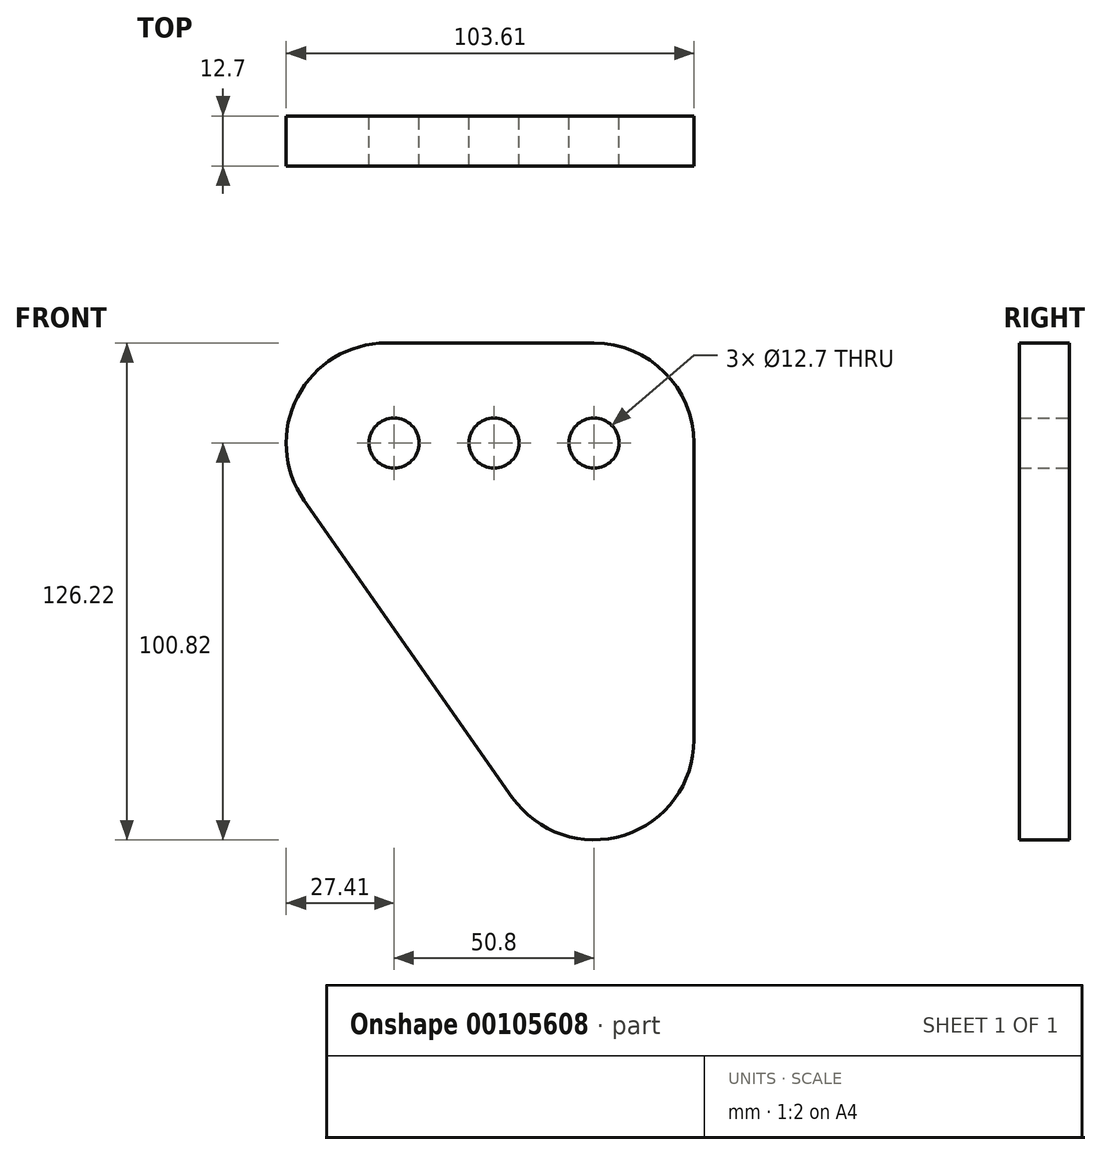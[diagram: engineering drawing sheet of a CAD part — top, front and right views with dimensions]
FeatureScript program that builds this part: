
annotation { "Feature Type Name" : "Feature", "Feature Type Description" : "" }
export const myFeature = defineFeature(function(context is Context, id is Id, definition is map)
    precondition{}
    {
        {
            var Q0;
            Q0=qCreatedBy(makeId("Front.planeOp"),FACE);
            var sketch = newSketch(context, id + "F0", { "sketchPlane" : qUnion([Q0])});
            skLineSegment(sketch, "E0", {"start": v(-127, 0) * mm, "end": v(0, 0) * mm});
            skLineSegment(sketch, "E1", {"start": v(0, 0) * mm, "end": v(0, -181.37) * mm});
            skLineSegment(sketch, "E2", {"start": v(0, -181.37) * mm, "end": v(-127, 0) * mm});
            skCircle(sketch, "E3", {"center": v(-25.4, -25.4) * mm, "radius": 6.35 * mm});
            skCircle(sketch, "E4", {"center": v(-50.8, -25.4) * mm, "radius": 6.35 * mm});
            skCircle(sketch, "E5", {"center": v(-76.2, -25.4) * mm, "radius": 6.35 * mm});
            skLineSegment(sketch, "E6", {"start": v(-76.2, -25.4) * mm, "end": v(-25.4, -25.4) * mm});
            skSolve(sketch);
        }
        {
            var Q0;
            Q0=makeQuery(id+"F0.imprint","IMPRINT",FACE,{"disambiguationData":[TD([[makeQuery(id+"F0.imprint","IMPRINT",EDGE,{"derivedFrom":sQuery(id+"F0.wireOp",EDGE,"E0")}),-1.0]])]});
            extrude(context, id + "F1", {"entities" : qUnion([Q0]), "endBound" : BoundingType.SYMMETRIC, "depth" : 12.7 * mm});
        }
        {
            var Q0;
            Q0=makeQuery(id+"F1.opExtrude","SWEPT_EDGE",EDGE,{"disambiguationData":[OSD([sQuery(id+"F0.wireOp",EDGE,"E0"),sQuery(id+"F0.wireOp",EDGE,"E1")])]});
            var Q1;
            Q1=makeQuery(id+"F1.opExtrude","SWEPT_EDGE",EDGE,{"disambiguationData":[OSD([sQuery(id+"F0.wireOp",EDGE,"E0"),sQuery(id+"F0.wireOp",EDGE,"E2")])]});
            var Q2;
            Q2=makeQuery(id+"F1.opExtrude","SWEPT_EDGE",EDGE,{"disambiguationData":[OSD([sQuery(id+"F0.wireOp",EDGE,"E1"),sQuery(id+"F0.wireOp",EDGE,"E2")])]});
            fillet(context, id + "F2", {"entities" : qUnion([Q0, Q1, Q2]), "radius" : 25.4 * mm, "tangentPropagation" : true, "allowEdgeOverflow" : false});
        }
    });
